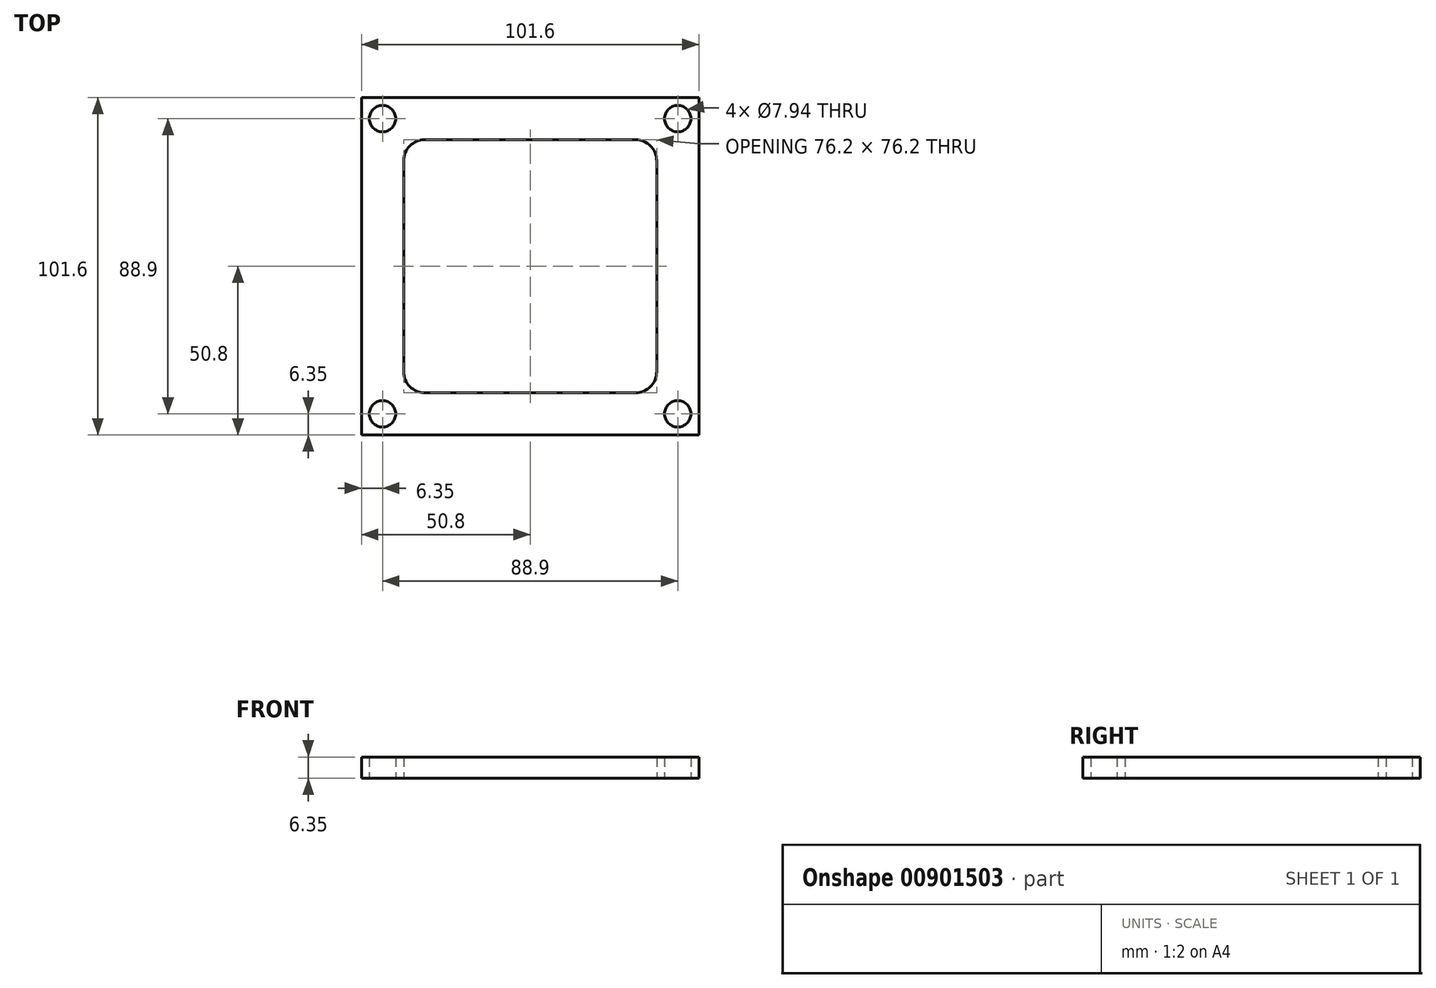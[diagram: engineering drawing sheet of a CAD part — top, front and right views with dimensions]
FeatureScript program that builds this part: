
annotation { "Feature Type Name" : "Feature", "Feature Type Description" : "" }
export const myFeature = defineFeature(function(context is Context, id is Id, definition is map)
    precondition{}
    {
        {
            var Q0;
            Q0=qCreatedBy(makeId("Top.planeOp"),FACE);
            var sketch = newSketch(context, id + "F0", { "sketchPlane" : qUnion([Q0])});
            skLineSegment(sketch, "E0.bottom", {"start": v(0, 0) * mm, "end": v(101.6, 0) * mm});
            skLineSegment(sketch, "E0.top", {"start": v(0, 101.6) * mm, "end": v(101.6, 101.6) * mm});
            skLineSegment(sketch, "E0.left", {"start": v(0, 0) * mm, "end": v(0, 101.6) * mm});
            skLineSegment(sketch, "E0.right", {"start": v(101.6, 0) * mm, "end": v(101.6, 101.6) * mm});
            skLineSegment(sketch, "E1.bottom", {"start": v(19.05, 12.7) * mm, "end": v(82.55, 12.7) * mm});
            skLineSegment(sketch, "E1.top", {"start": v(19.05, 88.9) * mm, "end": v(82.55, 88.9) * mm});
            skLineSegment(sketch, "E1.left", {"start": v(12.7, 19.05) * mm, "end": v(12.7, 82.55) * mm});
            skLineSegment(sketch, "E1.right", {"start": v(88.9, 19.05) * mm, "end": v(88.9, 82.55) * mm});
            skPoint(sketch, "E2.visualSharp", {"position": v(12.7, 12.7) * mm});
            skArc(sketch, "E2.filletArc", {"start": v(12.7, 19.05) * mm, "mid": v(14.56, 14.56) * mm, "end": v(19.05, 12.7) * mm});
            skPoint(sketch, "E3.visualSharp", {"position": v(88.9, 12.7) * mm});
            skArc(sketch, "E3.filletArc", {"start": v(82.55, 12.7) * mm, "mid": v(87.04, 14.56) * mm, "end": v(88.9, 19.05) * mm});
            skPoint(sketch, "E4.visualSharp", {"position": v(88.9, 88.9) * mm});
            skArc(sketch, "E4.filletArc", {"start": v(88.9, 82.55) * mm, "mid": v(87.04, 87.04) * mm, "end": v(82.55, 88.9) * mm});
            skPoint(sketch, "E5.visualSharp", {"position": v(12.7, 88.9) * mm});
            skArc(sketch, "E5.filletArc", {"start": v(19.05, 88.9) * mm, "mid": v(14.56, 87.04) * mm, "end": v(12.7, 82.55) * mm});
            skLineSegment(sketch, "E6", {"start": v(88.9, 12.7) * mm, "end": v(101.6, 0) * mm, "construction": true});
            skLineSegment(sketch, "E7", {"start": v(12.7, 12.7) * mm, "end": v(0, 0) * mm, "construction": true});
            skLineSegment(sketch, "E8", {"start": v(6.35, 6.35) * mm, "end": v(95.25, 6.35) * mm, "construction": true});
            skLineSegment(sketch, "E9", {"start": v(0, 101.6) * mm, "end": v(12.7, 88.9) * mm, "construction": true});
            skLineSegment(sketch, "E10", {"start": v(88.9, 88.9) * mm, "end": v(101.6, 101.6) * mm, "construction": true});
            skLineSegment(sketch, "E11", {"start": v(95.25, 95.25) * mm, "end": v(6.35, 95.25) * mm, "construction": true});
            skLineSegment(sketch, "E12", {"start": v(6.35, 95.25) * mm, "end": v(6.35, 6.35) * mm, "construction": true});
            skLineSegment(sketch, "E13", {"start": v(95.25, 6.35) * mm, "end": v(95.25, 95.25) * mm, "construction": true});
            skCircle(sketch, "E14", {"center": v(6.35, 95.25) * mm, "radius": 3.97 * mm});
            skCircle(sketch, "E15.0.1.0", {"center": v(6.35, 6.35) * mm, "radius": 3.97 * mm});
            skCircle(sketch, "E15.1.0.0", {"center": v(95.25, 95.25) * mm, "radius": 3.97 * mm});
            skCircle(sketch, "E15.1.1.0", {"center": v(95.25, 6.35) * mm, "radius": 3.97 * mm});
            skLineSegment(sketch, "E15.direction1", {"start": v(6.35, 95.25) * mm, "end": v(95.25, 95.25) * mm, "construction": true});
            skLineSegment(sketch, "E16.bottom", {"start": v(2.38, 2.38) * mm, "end": v(10.32, 2.38) * mm, "construction": true});
            skLineSegment(sketch, "E16.top", {"start": v(2.38, 10.32) * mm, "end": v(10.32, 10.32) * mm, "construction": true});
            skLineSegment(sketch, "E16.left", {"start": v(2.38, 2.38) * mm, "end": v(2.38, 10.32) * mm, "construction": true});
            skLineSegment(sketch, "E16.right", {"start": v(10.32, 2.38) * mm, "end": v(10.32, 10.32) * mm, "construction": true});
            skLineSegment(sketch, "E17.0.1.0", {"start": v(10.32, 91.28) * mm, "end": v(10.32, 99.22) * mm, "construction": true});
            skLineSegment(sketch, "E17.0.1.1", {"start": v(2.38, 99.22) * mm, "end": v(10.32, 99.22) * mm, "construction": true});
            skLineSegment(sketch, "E17.0.1.2", {"start": v(2.38, 91.28) * mm, "end": v(2.38, 99.22) * mm, "construction": true});
            skLineSegment(sketch, "E17.0.1.3", {"start": v(2.38, 91.28) * mm, "end": v(10.32, 91.28) * mm, "construction": true});
            skLineSegment(sketch, "E17.1.0.0", {"start": v(99.22, 2.38) * mm, "end": v(99.22, 10.32) * mm, "construction": true});
            skLineSegment(sketch, "E17.1.0.1", {"start": v(91.28, 10.32) * mm, "end": v(99.22, 10.32) * mm, "construction": true});
            skLineSegment(sketch, "E17.1.0.2", {"start": v(91.28, 2.38) * mm, "end": v(91.28, 10.32) * mm, "construction": true});
            skLineSegment(sketch, "E17.1.0.3", {"start": v(91.28, 2.38) * mm, "end": v(99.22, 2.38) * mm, "construction": true});
            skLineSegment(sketch, "E17.1.1.0", {"start": v(99.22, 91.28) * mm, "end": v(99.22, 99.22) * mm, "construction": true});
            skLineSegment(sketch, "E17.1.1.1", {"start": v(91.28, 99.22) * mm, "end": v(99.22, 99.22) * mm, "construction": true});
            skLineSegment(sketch, "E17.1.1.2", {"start": v(91.28, 91.28) * mm, "end": v(91.28, 99.22) * mm, "construction": true});
            skLineSegment(sketch, "E17.1.1.3", {"start": v(91.28, 91.28) * mm, "end": v(99.22, 91.28) * mm, "construction": true});
            skSolve(sketch);
        }
        {
            var Q0;
            Q0=makeQuery(id+"F0.imprint","IMPRINT",FACE,{"disambiguationData":[TD([[makeQuery(id+"F0.imprint","IMPRINT",EDGE,{"derivedFrom":sQuery(id+"F0.wireOp",EDGE,"E0.bottom")}),1.0]])]});
            extrude(context, id + "F1", {"entities" : qUnion([Q0]), "depth" : 6.35 * mm, "offsetDistance" : 25.4 * mm});
        }
    });
